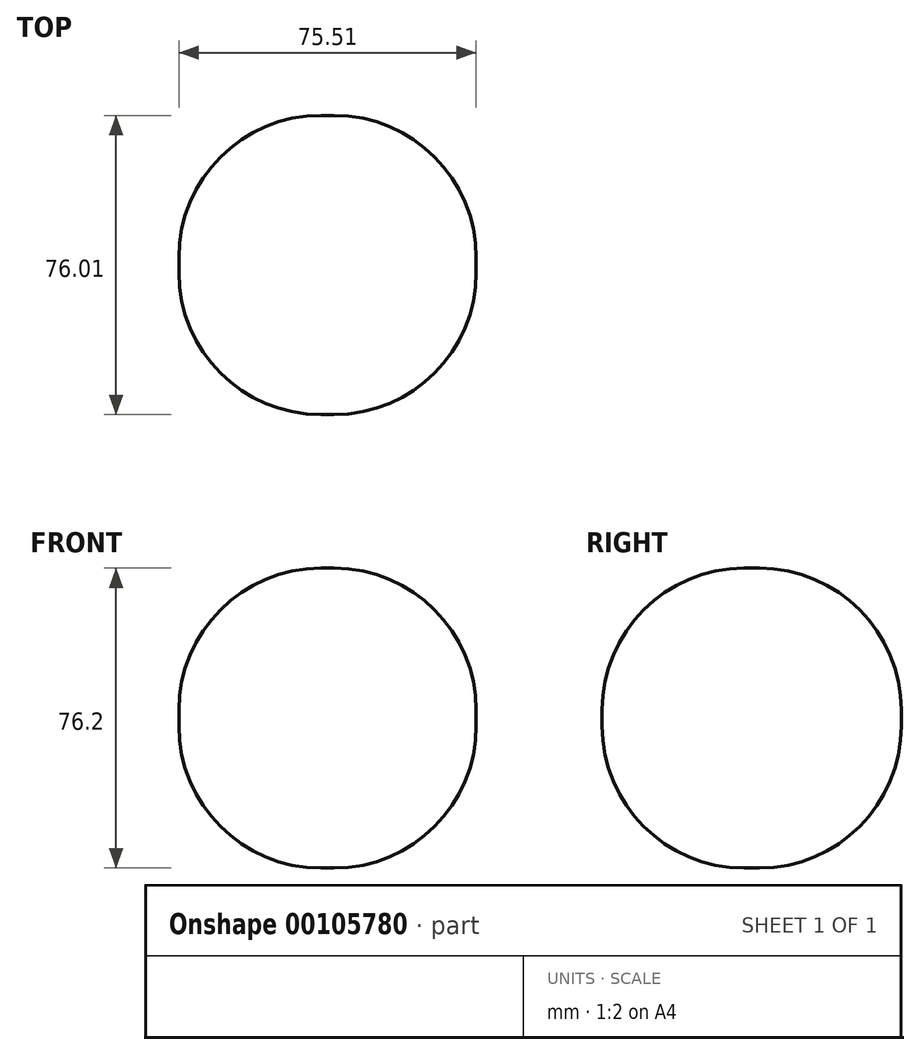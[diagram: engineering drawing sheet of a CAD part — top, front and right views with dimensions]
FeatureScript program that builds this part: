
annotation { "Feature Type Name" : "Feature", "Feature Type Description" : "" }
export const myFeature = defineFeature(function(context is Context, id is Id, definition is map)
    precondition{}
    {
        {
            var Q0;
            Q0=qCreatedBy(makeId("Top.planeOp"),FACE);
            var sketch = newSketch(context, id + "F0", { "sketchPlane" : qUnion([Q0])});
            skLineSegment(sketch, "E0.bottom", {"start": v(0, 0) * mm, "end": v(75.51, 0) * mm});
            skLineSegment(sketch, "E0.top", {"start": v(0, 76) * mm, "end": v(75.51, 76) * mm});
            skLineSegment(sketch, "E0.left", {"start": v(0, 0) * mm, "end": v(0, 76) * mm});
            skLineSegment(sketch, "E0.right", {"start": v(75.51, 0) * mm, "end": v(75.51, 76) * mm});
            skSolve(sketch);
        }
        {
            var Q0;
            Q0=makeQuery(id+"F0.imprint","IMPRINT",FACE,{"disambiguationData":[TD([[makeQuery(id+"F0.imprint","IMPRINT",EDGE,{"derivedFrom":sQuery(id+"F0.wireOp",EDGE,"E0.bottom")}),1.0]])]});
            extrude(context, id + "F1", {"entities" : qUnion([Q0]), "depth" : 76.2 * mm});
        }
        {
            var Q0;
            Q0=makeQuery(id+"F1.opExtrude","SWEPT_EDGE",EDGE,{"disambiguationData":[OSD([sQuery(id+"F0.wireOp",EDGE,"E0.bottom"),sQuery(id+"F0.wireOp",EDGE,"E0.left")])]});
            var Q1;
            Q1=makeQuery(id+"F1.opExtrude","CAP_EDGE",EDGE,{"disambiguationData":[OSD([sQuery(id+"F0.wireOp",EDGE,"E0.right")])],"isStart":true});
            var Q2;
            Q2=makeQuery(id+"F1.opExtrude","CAP_EDGE",EDGE,{"disambiguationData":[OSD([sQuery(id+"F0.wireOp",EDGE,"E0.bottom")])],"isStart":true});
            var Q3;
            Q3=makeQuery(id+"F1.opExtrude","SWEPT_EDGE",EDGE,{"disambiguationData":[OSD([sQuery(id+"F0.wireOp",EDGE,"E0.top"),sQuery(id+"F0.wireOp",EDGE,"E0.right")])]});
            var Q4;
            Q4=makeQuery(id+"F1.opExtrude","CAP_FACE",FACE,{"disambiguationData":[OSD([sQuery(id+"F0.wireOp",EDGE,"E0.bottom"),sQuery(id+"F0.wireOp",EDGE,"E0.top"),sQuery(id+"F0.wireOp",EDGE,"E0.left"),sQuery(id+"F0.wireOp",EDGE,"E0.right")])],"isStart":false});
            var Q5;
            Q5=makeQuery(id+"F1.opExtrude","SWEPT_EDGE",EDGE,{"disambiguationData":[OSD([sQuery(id+"F0.wireOp",EDGE,"E0.top"),sQuery(id+"F0.wireOp",EDGE,"E0.left")])]});
            var Q6;
            Q6=makeQuery(id+"F1.opExtrude","CAP_EDGE",EDGE,{"disambiguationData":[OSD([sQuery(id+"F0.wireOp",EDGE,"E0.top")])],"isStart":true});
            var Q7;
            Q7=makeQuery(id+"F1.opExtrude","CAP_EDGE",EDGE,{"disambiguationData":[OSD([sQuery(id+"F0.wireOp",EDGE,"E0.left")])],"isStart":true});
            var Q8;
            Q8=makeQuery(id+"F1.opExtrude","SWEPT_EDGE",EDGE,{"disambiguationData":[OSD([sQuery(id+"F0.wireOp",EDGE,"E0.bottom"),sQuery(id+"F0.wireOp",EDGE,"E0.right")])]});
            fillet(context, id + "F2", {"entities" : qUnion([Q0, Q1, Q2, Q3, Q4, Q5, Q6, Q7, Q8]), "radius" : 36.07 * mm, "tangentPropagation" : true, "allowEdgeOverflow" : false});
        }
    });
